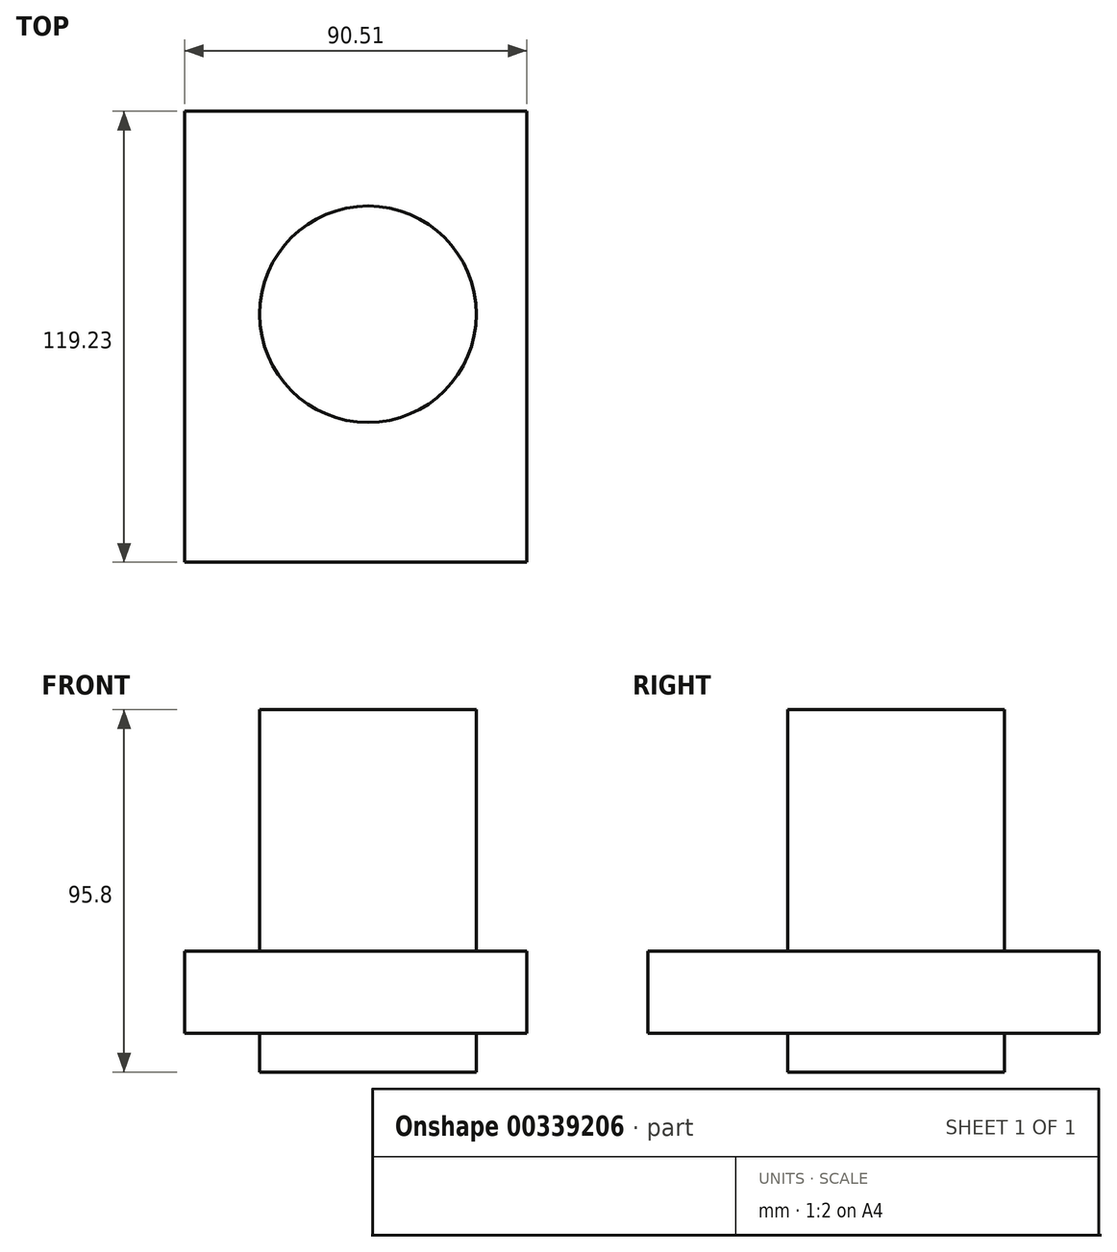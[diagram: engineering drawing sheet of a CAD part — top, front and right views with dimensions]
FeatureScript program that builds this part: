
annotation { "Feature Type Name" : "Feature", "Feature Type Description" : "" }
export const myFeature = defineFeature(function(context is Context, id is Id, definition is map)
    precondition{}
    {
        {
            var Q0;
            Q0=qCreatedBy(makeId("Top.planeOp"),FACE);
            var sketch = newSketch(context, id + "F0", { "sketchPlane" : qUnion([Q0])});
            skCircle(sketch, "E0", {"center": v(24.5, -28.25) * mm, "radius": 28.62 * mm});
            skPoint(sketch, "E0.first.point", {"position": v(19.91, 0) * mm});
            skPoint(sketch, "E0.second.point", {"position": v(0, -43.05) * mm});
            skPoint(sketch, "E0.third.point", {"position": v(52.24, -35.26) * mm});
            skSolve(sketch);
        }
        {
            var Q0;
            Q0 = qSketchRegion(id + "F0", true);
            extrude(context, id + "F1", {"entities" : qUnion([Q0]), "depth" : 95.8 * mm});
        }
        {
            var Q0;
            Q0=qCreatedBy(makeId("Front.planeOp"),FACE);
            var sketch = newSketch(context, id + "F2", { "sketchPlane" : qUnion([Q0])});
            skLineSegment(sketch, "E1.bottom", {"start": v(66.5, 31.98) * mm, "end": v(-24, 31.98) * mm});
            skLineSegment(sketch, "E1.top", {"start": v(66.5, 10.18) * mm, "end": v(-24, 10.18) * mm});
            skLineSegment(sketch, "E1.left", {"start": v(66.5, 31.98) * mm, "end": v(66.5, 10.18) * mm});
            skLineSegment(sketch, "E1.right", {"start": v(-24, 31.98) * mm, "end": v(-24, 10.18) * mm});
            skSolve(sketch);
        }
        {
            var Q0;
            Q0 = qSketchRegion(id + "F2", true);
            extrude(context, id + "F3", {"entities" : qUnion([Q0]), "operationType" : NewBodyOperationType.ADD, "depth" : 93.83 * mm, "hasSecondDirection" : true, "secondDirectionOppositeDirection" : true, "secondDirectionDepth" : 25.4 * mm});
        }
    });
